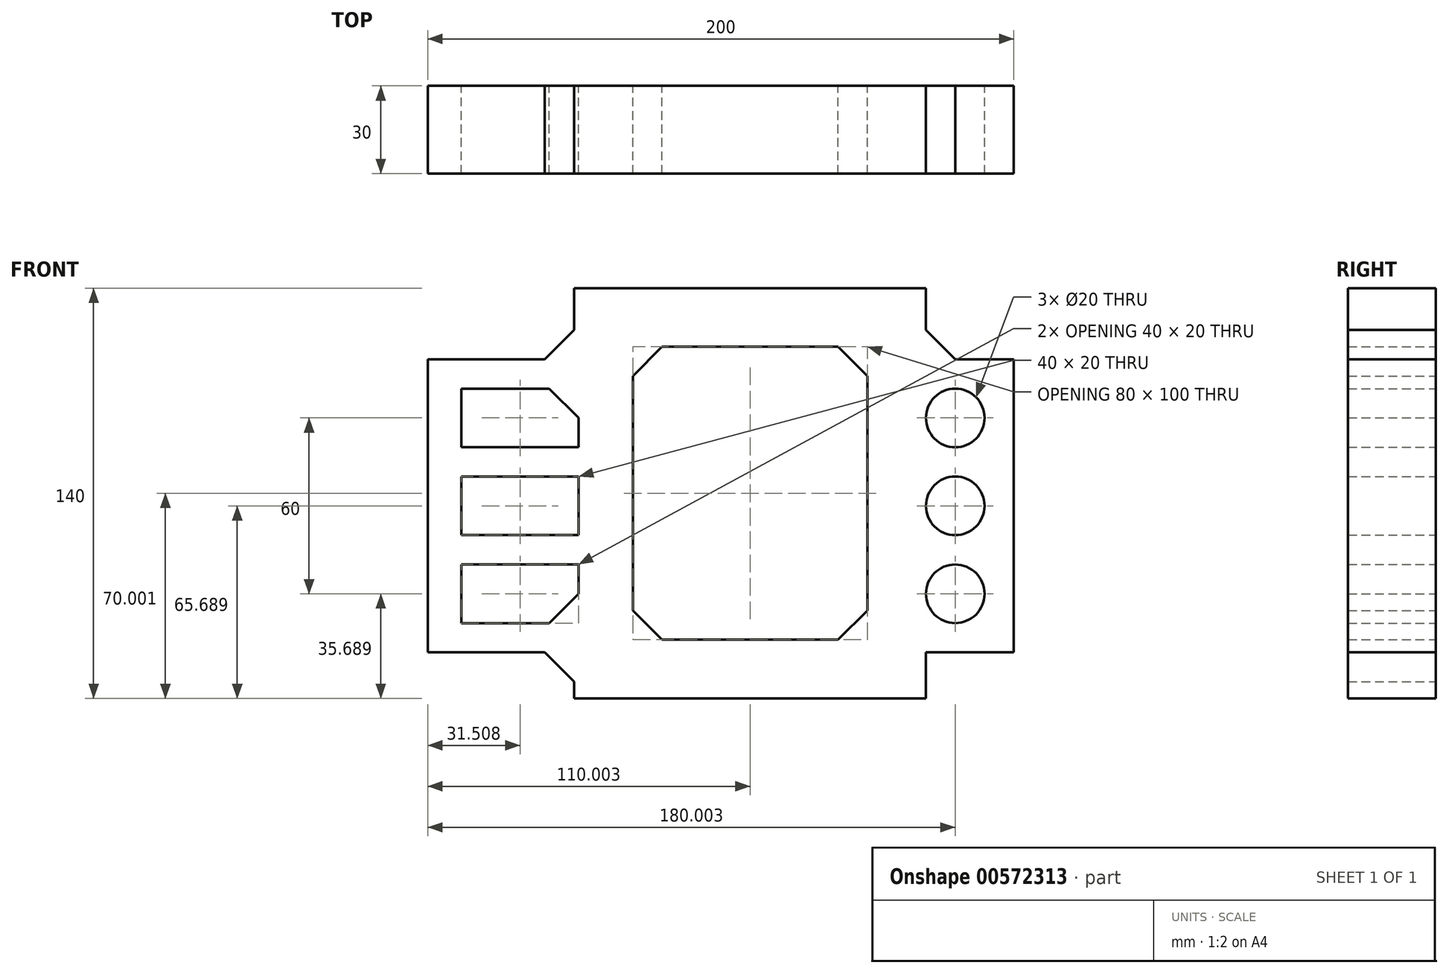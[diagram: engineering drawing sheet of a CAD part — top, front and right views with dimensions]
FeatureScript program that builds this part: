
annotation { "Feature Type Name" : "Feature", "Feature Type Description" : "" }
export const myFeature = defineFeature(function(context is Context, id is Id, definition is map)
    precondition{}
    {
        {
            var Q0;
            Q0=qCreatedBy(makeId("Front.planeOp"),FACE);
            var sketch = newSketch(context, id + "F0", { "sketchPlane" : qUnion([Q0])});
            skLineSegment(sketch, "E0", {"start": v(-53.39, 45.14) * mm, "end": v(-93.39, 45.14) * mm});
            skLineSegment(sketch, "E1", {"start": v(-93.39, 45.14) * mm, "end": v(-93.39, -54.86) * mm});
            skLineSegment(sketch, "E2", {"start": v(-93.39, -54.86) * mm, "end": v(-53.39, -54.86) * mm});
            skLineSegment(sketch, "E3", {"start": v(-43.39, -64.86) * mm, "end": v(-43.39, -70.55) * mm});
            skLineSegment(sketch, "E4", {"start": v(-43.39, -70.55) * mm, "end": v(66.61, -70.55) * mm});
            skLineSegment(sketch, "E5", {"start": v(76.61, -64.86) * mm, "end": v(76.61, -60.55) * mm});
            skLineSegment(sketch, "E6", {"start": v(86.61, -54.86) * mm, "end": v(96.61, -54.86) * mm});
            skLineSegment(sketch, "E7", {"start": v(106.61, -44.86) * mm, "end": v(106.61, 35.14) * mm});
            skLineSegment(sketch, "E8", {"start": v(96.61, 45.14) * mm, "end": v(86.61, 45.14) * mm});
            skLineSegment(sketch, "E9", {"start": v(76.61, 55.14) * mm, "end": v(76.61, 59.45) * mm});
            skLineSegment(sketch, "E10", {"start": v(66.61, 69.45) * mm, "end": v(-33.39, 69.45) * mm});
            skLineSegment(sketch, "E11", {"start": v(-43.39, 59.45) * mm, "end": v(-43.39, 55.14) * mm});
            skCircle(sketch, "E12", {"center": v(86.61, 25.14) * mm, "radius": 10 * mm});
            skCircle(sketch, "E13", {"center": v(86.61, -4.86) * mm, "radius": 10 * mm});
            skCircle(sketch, "E14", {"center": v(86.61, -34.86) * mm, "radius": 10 * mm});
            skLineSegment(sketch, "E15", {"start": v(-81.88, 35.14) * mm, "end": v(-51.88, 35.14) * mm});
            skLineSegment(sketch, "E16", {"start": v(-41.88, 25.14) * mm, "end": v(-41.88, 15.14) * mm});
            skLineSegment(sketch, "E17", {"start": v(-41.88, 15.14) * mm, "end": v(-81.88, 15.14) * mm});
            skLineSegment(sketch, "E18", {"start": v(-81.88, 15.14) * mm, "end": v(-81.88, 35.14) * mm});
            skLineSegment(sketch, "E19", {"start": v(-81.88, 5.14) * mm, "end": v(-51.88, 5.14) * mm});
            skLineSegment(sketch, "E20", {"start": v(-41.88, -4.86) * mm, "end": v(-41.88, -14.86) * mm});
            skLineSegment(sketch, "E21", {"start": v(-41.88, -14.86) * mm, "end": v(-81.88, -14.86) * mm});
            skLineSegment(sketch, "E22", {"start": v(-81.88, -14.86) * mm, "end": v(-81.88, 5.14) * mm});
            skLineSegment(sketch, "E23", {"start": v(-81.88, -24.86) * mm, "end": v(-51.88, -24.86) * mm});
            skLineSegment(sketch, "E24", {"start": v(-41.88, -34.86) * mm, "end": v(-41.88, -34.86) * mm});
            skLineSegment(sketch, "E25", {"start": v(-51.88, -44.86) * mm, "end": v(-81.88, -44.86) * mm});
            skLineSegment(sketch, "E26", {"start": v(-81.88, -44.86) * mm, "end": v(-81.88, -24.86) * mm});
            skLineSegment(sketch, "E27", {"start": v(-13.39, 49.45) * mm, "end": v(46.61, 49.45) * mm});
            skLineSegment(sketch, "E28", {"start": v(56.61, 39.45) * mm, "end": v(56.61, 24.45) * mm});
            skLineSegment(sketch, "E29", {"start": v(-23.39, 24.45) * mm, "end": v(-23.39, 39.45) * mm});
            skLineSegment(sketch, "E30", {"start": v(56.61, -0.55) * mm, "end": v(56.61, -40.55) * mm});
            skLineSegment(sketch, "E31", {"start": v(46.61, -50.55) * mm, "end": v(-13.39, -50.55) * mm});
            skLineSegment(sketch, "E32", {"start": v(-23.39, -40.55) * mm, "end": v(-23.39, -0.55) * mm});
            skPoint(sketch, "E33.visualSharp", {"position": v(-41.88, 35.14) * mm});
            skPoint(sketch, "E34.visualSharp", {"position": v(-41.88, 5.14) * mm});
            skPoint(sketch, "E35.visualSharp", {"position": v(-41.88, -24.86) * mm});
            skPoint(sketch, "E36.visualSharp", {"position": v(76.61, -54.86) * mm});
            skPoint(sketch, "E37.visualSharp", {"position": v(106.61, -54.86) * mm});
            skPoint(sketch, "E38.visualSharp", {"position": v(106.61, 45.14) * mm});
            skPoint(sketch, "E39.visualSharp", {"position": v(76.61, 45.14) * mm});
            skPoint(sketch, "E40.visualSharp", {"position": v(76.61, 69.45) * mm});
            skPoint(sketch, "E41.visualSharp", {"position": v(76.61, -70.55) * mm});
            skPoint(sketch, "E42.visualSharp", {"position": v(-43.39, 45.14) * mm});
            skPoint(sketch, "E43.visualSharp", {"position": v(-43.39, 69.45) * mm});
            skPoint(sketch, "E44.visualSharp", {"position": v(-23.39, 49.45) * mm});
            skPoint(sketch, "E45.visualSharp", {"position": v(56.61, 49.45) * mm});
            skPoint(sketch, "E46.visualSharp", {"position": v(-23.39, -50.55) * mm});
            skPoint(sketch, "E47.visualSharp", {"position": v(56.61, -50.55) * mm});
            skLineSegment(sketch, "E48", {"start": v(-23.39, 24.45) * mm, "end": v(-23.39, -0.55) * mm});
            skLineSegment(sketch, "E49", {"start": v(56.61, 24.45) * mm, "end": v(56.61, -0.55) * mm});
            skLineSegment(sketch, "E50", {"start": v(-23.39, 39.45) * mm, "end": v(-13.39, 49.45) * mm});
            skLineSegment(sketch, "E51", {"start": v(46.61, 49.45) * mm, "end": v(56.61, 39.45) * mm});
            skLineSegment(sketch, "E52", {"start": v(-23.39, -40.55) * mm, "end": v(-13.39, -50.55) * mm});
            skLineSegment(sketch, "E53", {"start": v(46.61, -50.55) * mm, "end": v(56.61, -40.55) * mm});
            skLineSegment(sketch, "E54", {"start": v(-51.88, 35.14) * mm, "end": v(-41.88, 25.14) * mm});
            skLineSegment(sketch, "E55", {"start": v(-51.88, 5.14) * mm, "end": v(-41.88, 5.14) * mm});
            skLineSegment(sketch, "E56", {"start": v(-41.88, -4.86) * mm, "end": v(-41.88, 5.14) * mm});
            skLineSegment(sketch, "E57", {"start": v(-53.39, 45.14) * mm, "end": v(-43.39, 55.14) * mm});
            skLineSegment(sketch, "E58", {"start": v(76.61, 55.14) * mm, "end": v(86.61, 45.14) * mm});
            skLineSegment(sketch, "E59", {"start": v(96.61, 45.14) * mm, "end": v(106.61, 45.14) * mm});
            skLineSegment(sketch, "E60", {"start": v(106.61, 35.14) * mm, "end": v(106.61, 45.14) * mm});
            skLineSegment(sketch, "E61", {"start": v(96.61, -54.86) * mm, "end": v(106.61, -54.86) * mm});
            skLineSegment(sketch, "E62", {"start": v(106.61, -44.86) * mm, "end": v(106.61, -54.86) * mm});
            skLineSegment(sketch, "E63", {"start": v(86.61, -54.86) * mm, "end": v(76.61, -54.86) * mm});
            skLineSegment(sketch, "E64", {"start": v(76.61, -54.86) * mm, "end": v(76.61, -70.55) * mm});
            skLineSegment(sketch, "E65", {"start": v(76.61, -70.55) * mm, "end": v(66.61, -70.55) * mm});
            skLineSegment(sketch, "E66", {"start": v(-33.39, 69.45) * mm, "end": v(-43.39, 69.45) * mm});
            skLineSegment(sketch, "E67", {"start": v(-43.39, 59.45) * mm, "end": v(-43.39, 69.45) * mm});
            skLineSegment(sketch, "E68", {"start": v(66.61, 69.45) * mm, "end": v(76.61, 69.45) * mm});
            skLineSegment(sketch, "E69", {"start": v(76.61, 69.45) * mm, "end": v(76.61, 59.45) * mm});
            skPoint(sketch, "E70.visualSharp", {"position": v(-43.39, -54.86) * mm});
            skLineSegment(sketch, "E71", {"start": v(-53.39, -54.86) * mm, "end": v(-43.39, -64.86) * mm});
            skLineSegment(sketch, "E72", {"start": v(-41.88, -34.86) * mm, "end": v(-41.88, -24.86) * mm});
            skLineSegment(sketch, "E73", {"start": v(-51.88, -24.86) * mm, "end": v(-41.88, -24.86) * mm});
            skLineSegment(sketch, "E74", {"start": v(-41.88, -34.86) * mm, "end": v(-51.88, -44.86) * mm});
            skSolve(sketch);
        }
        {
            var Q0;
            Q0=makeQuery(id+"F0.imprint","IMPRINT",FACE,{"disambiguationData":[TD([[makeQuery(id+"F0.imprint","IMPRINT",EDGE,{"derivedFrom":sQuery(id+"F0.wireOp",EDGE,"E0")}),1.0]])]});
            extrude(context, id + "F1", {"entities" : qUnion([Q0]), "depth" : 30 * mm, "offsetDistance" : 25 * mm});
        }
    });
